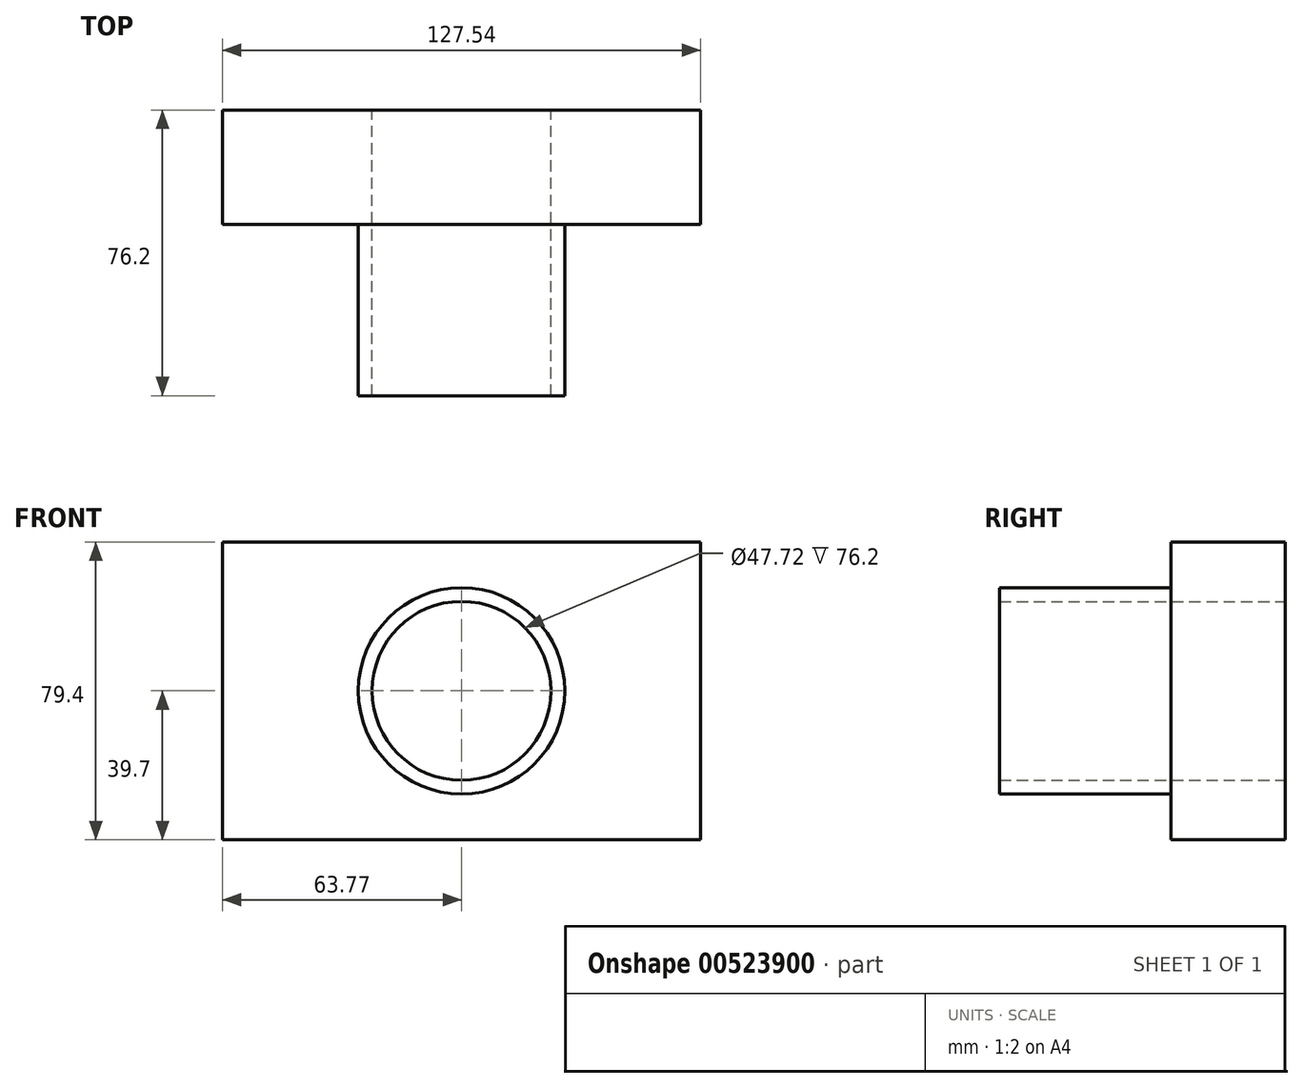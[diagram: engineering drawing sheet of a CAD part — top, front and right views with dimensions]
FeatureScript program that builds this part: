
annotation { "Feature Type Name" : "Feature", "Feature Type Description" : "" }
export const myFeature = defineFeature(function(context is Context, id is Id, definition is map)
    precondition{}
    {
        {
            var Q0;
            Q0=qCreatedBy(makeId("Front.planeOp"),FACE);
            var sketch = newSketch(context, id + "F0", { "sketchPlane" : qUnion([Q0])});
            skLineSegment(sketch, "E0.bottom", {"start": v(63.77, -39.7) * mm, "end": v(-63.77, -39.7) * mm});
            skLineSegment(sketch, "E0.top", {"start": v(63.77, 39.7) * mm, "end": v(-63.77, 39.7) * mm});
            skLineSegment(sketch, "E0.left", {"start": v(63.77, -39.7) * mm, "end": v(63.77, 39.7) * mm});
            skLineSegment(sketch, "E0.right", {"start": v(-63.77, -39.7) * mm, "end": v(-63.77, 39.7) * mm});
            skPoint(sketch, "E0.middle", {"position": v(0, 0) * mm});
            skSolve(sketch);
        }
        {
            var Q0;
            Q0=makeQuery(id+"F0.imprint","IMPRINT",FACE,{"disambiguationData":[TD([[makeQuery(id+"F0.imprint","IMPRINT",EDGE,{"derivedFrom":sQuery(id+"F0.wireOp",EDGE,"E0.bottom")}),-1.0]])]});
            extrude(context, id + "F1", {"entities" : qUnion([Q0]), "endBound" : BoundingType.SYMMETRIC, "depth" : 30.48 * mm, "offsetDistance" : 25.4 * mm});
        }
        {
            var Q0;
            Q0=makeQuery(id+"F1.opExtrude","CAP_FACE",FACE,{"disambiguationData":[OSD([sQuery(id+"F0.wireOp",EDGE,"E0.bottom"),sQuery(id+"F0.wireOp",EDGE,"E0.top"),sQuery(id+"F0.wireOp",EDGE,"E0.left"),sQuery(id+"F0.wireOp",EDGE,"E0.right")])],"isStart":false});
            var sketch = newSketch(context, id + "F2", { "sketchPlane" : qUnion([Q0])});
            skCircle(sketch, "E1", {"center": v(0, 0) * mm, "radius": 27.53 * mm});
            skCircle(sketch, "E2", {"center": v(0, 0) * mm, "radius": 23.86 * mm});
            skSolve(sketch);
        }
        {
            var Q0;
            Q0=makeQuery(id+"F2.imprint","IMPRINT",FACE,{"disambiguationData":[TD([[makeQuery(id+"F2.imprint","IMPRINT",EDGE,{"derivedFrom":sQuery(id+"F2.wireOp",EDGE,"E1")}),1.0]])]});
            extrude(context, id + "F3", {"entities" : qUnion([Q0]), "operationType" : NewBodyOperationType.ADD, "depth" : 45.72 * mm, "offsetDistance" : 25.4 * mm});
        }
        {
            var Q0;
            Q0=makeQuery(id+"F3.boolean.opBoolean","SPLIT",FACE,{"disambiguationData":[TD([makeQuery(id+"F3.opExtrude","SWEPT_FACE",FACE,{"disambiguationData":[OSD([sQuery(id+"F2.wireOp",EDGE,"E2")])]})])],"derivedFrom":makeQuery(id+"F1.opExtrude","CAP_FACE",FACE,{"disambiguationData":[OSD([sQuery(id+"F0.wireOp",EDGE,"E0.bottom"),sQuery(id+"F0.wireOp",EDGE,"E0.top"),sQuery(id+"F0.wireOp",EDGE,"E0.left"),sQuery(id+"F0.wireOp",EDGE,"E0.right")])],"isStart":false})});
            extrude(context, id + "F4", {"entities" : qUnion([Q0]), "operationType" : NewBodyOperationType.REMOVE, "oppositeDirection" : true, "depth" : 47 * mm, "offsetDistance" : 25.4 * mm});
        }
    });
